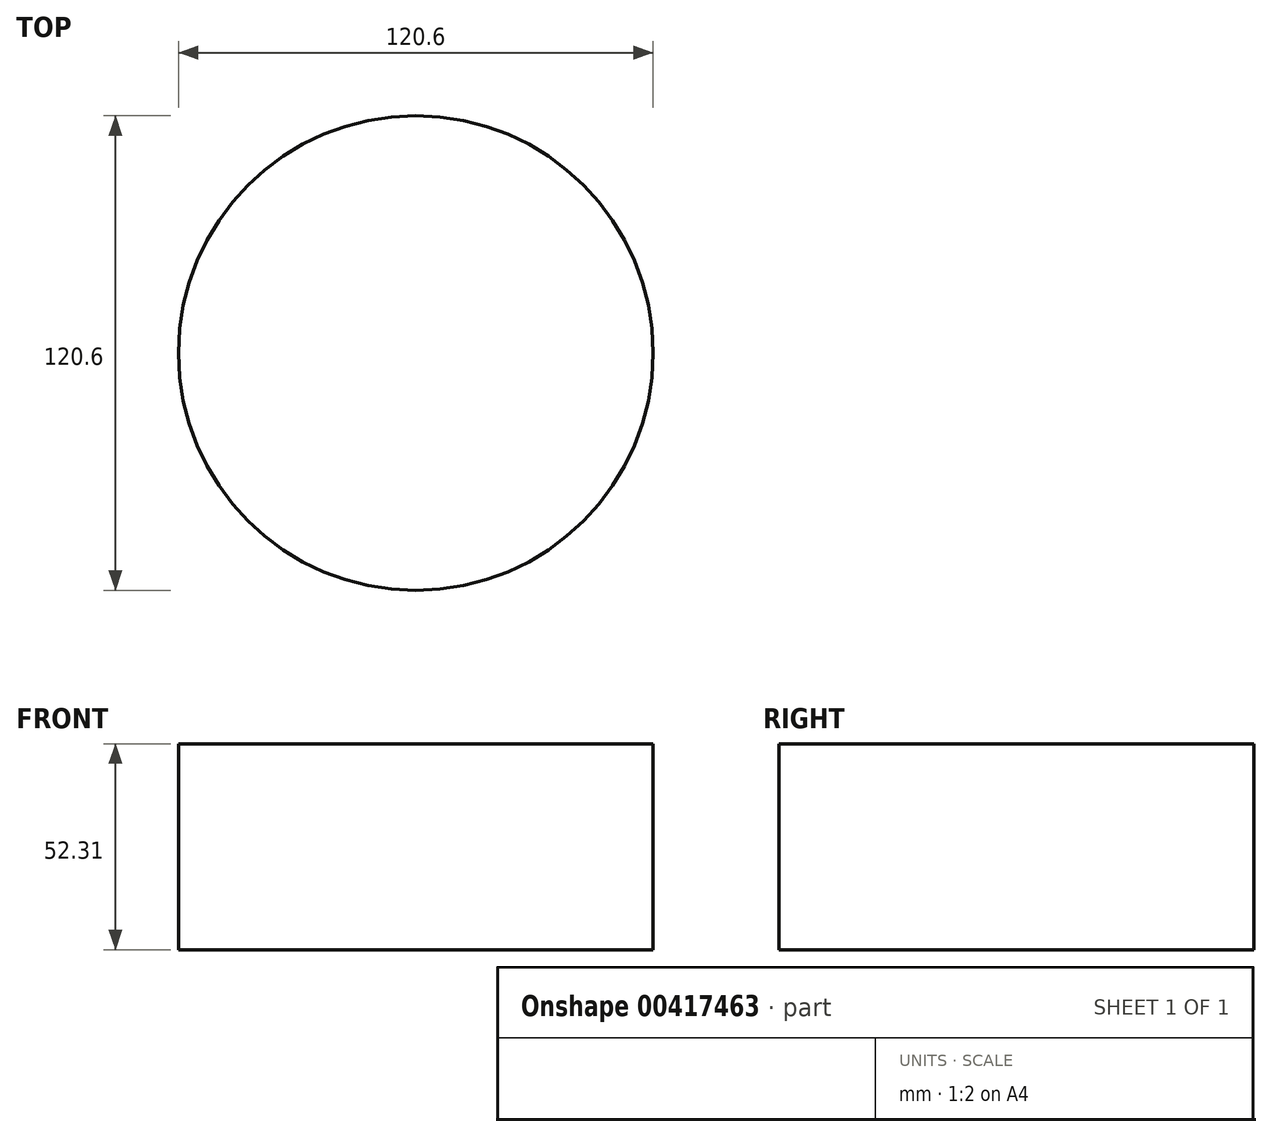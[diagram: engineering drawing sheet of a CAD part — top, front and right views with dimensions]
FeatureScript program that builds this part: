
annotation { "Feature Type Name" : "Feature", "Feature Type Description" : "" }
export const myFeature = defineFeature(function(context is Context, id is Id, definition is map)
    precondition{}
    {
        {
            var Q0;
            Q0=qCreatedBy(makeId("Top.planeOp"),FACE);
            var sketch = newSketch(context, id + "F0", { "sketchPlane" : qUnion([Q0])});
            skCircle(sketch, "E0", {"center": v(0, 0) * mm, "radius": 60.3 * mm});
            skSolve(sketch);
        }
        {
            var Q0;
            Q0=makeQuery(id+"F0.imprint","IMPRINT",FACE,{"disambiguationData":[TD([[makeQuery(id+"F0.imprint","IMPRINT",EDGE,{"derivedFrom":sQuery(id+"F0.wireOp",EDGE,"E0")}),1.0]])]});
            extrude(context, id + "F1", {"entities" : qUnion([Q0]), "depth" : 52.31 * mm});
        }
    });
